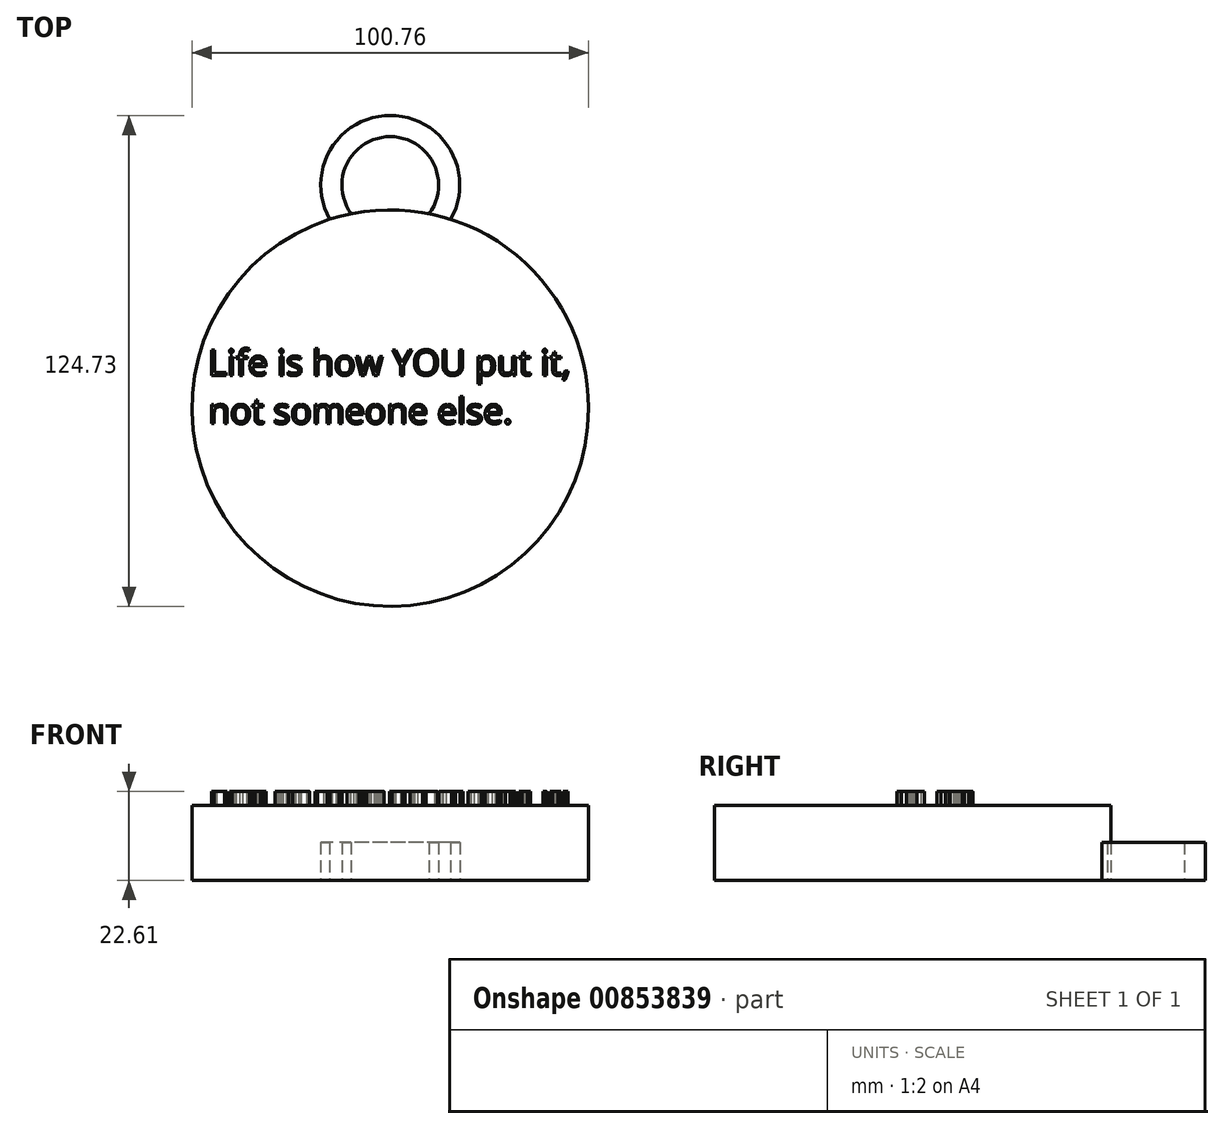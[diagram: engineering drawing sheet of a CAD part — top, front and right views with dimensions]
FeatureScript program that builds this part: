
annotation { "Feature Type Name" : "Feature", "Feature Type Description" : "" }
export const myFeature = defineFeature(function(context is Context, id is Id, definition is map)
    precondition{}
    {
        {
            var Q0;
            Q0=qCreatedBy(makeId("Top.planeOp"),FACE);
            var sketch = newSketch(context, id + "F0", { "sketchPlane" : qUnion([Q0])});
            skCircle(sketch, "E0", {"center": v(0, 0) * mm, "radius": 50.38 * mm});
            skSolve(sketch);
        }
        {
            var Q0;
            Q0 = qSketchRegion(id + "F0", true);
            extrude(context, id + "F1", {"entities" : qUnion([Q0]), "depth" : 19.05 * mm, "offsetDistance" : 25.4 * mm});
        }
        {
            var Q0;
            Q0=makeQuery(id+"F1.opExtrude","CAP_FACE",FACE,{"disambiguationData":[OSD([sQuery(id+"F0.wireOp",EDGE,"E0")])],"isStart":false});
            var sketch = newSketch(context, id + "F2", { "sketchPlane" : qUnion([Q0])});
            skText(sketch, "E1", { "text": "Life is how YOU put it,\nnot someone else.", "fontName": "OpenSans-Regular.ttf"});
            const initialGuessF2  = {"E1": [-0.04622, 0.00834, 1, 0, 0.0065]};
            skSetInitialGuess(sketch, initialGuessF2);
            skSolve(sketch);
        }
        {
            var Q0;
            Q0 = qSketchRegion(id + "F2", true);
            extrude(context, id + "F3", {"entities" : qUnion([Q0]), "operationType" : NewBodyOperationType.ADD, "depth" : 3.56 * mm, "offsetDistance" : 25.4 * mm});
        }
        {
            var Q0;
            Q0=qCreatedBy(makeId("Top.planeOp"),FACE);
            var sketch = newSketch(context, id + "F4", { "sketchPlane" : qUnion([Q0])});
            skCircle(sketch, "E2", {"center": v(0, 56.69) * mm, "radius": 17.66 * mm});
            skCircle(sketch, "E3", {"center": v(0, 56.69) * mm, "radius": 12.3 * mm});
            skSolve(sketch);
        }
        {
            var Q0;
            Q0 = qSketchRegion(id + "F4", true);
            var Q1;
            {var subQ0=sQuery(id+"F0.wireOp",EDGE,"E0");Q1=makeQuery(id+"F3.boolean.opBoolean","SPLIT",FACE,{"disambiguationData":[TD([makeQuery(id+"F1.opExtrude","SWEPT_FACE",FACE,{"disambiguationData":[OSD([subQ0])]})])],"derivedFrom":makeQuery(id+"F1.opExtrude","CAP_FACE",FACE,{"disambiguationData":[OSD([subQ0])],"isStart":false})});}
            extrude(context, id + "F5", {"entities" : qUnion([Q0]), "operationType" : NewBodyOperationType.ADD, "depth" : 9.65 * mm, "endBoundEntityFace" : qUnion([Q1]), "offsetDistance" : 25.4 * mm});
        }
    });
